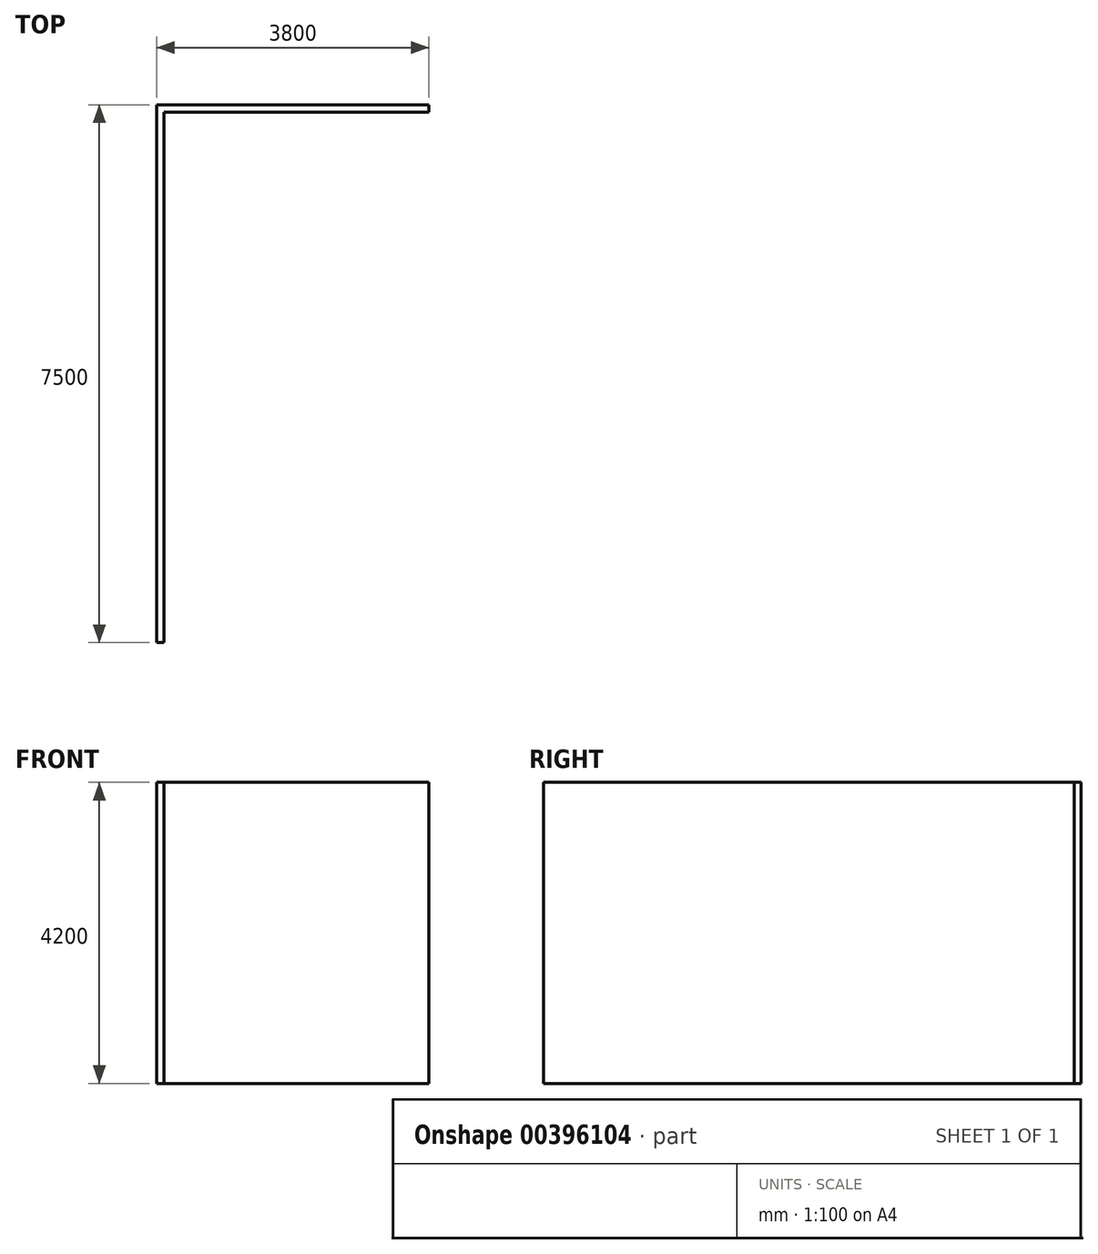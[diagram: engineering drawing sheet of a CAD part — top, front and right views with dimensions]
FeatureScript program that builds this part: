
annotation { "Feature Type Name" : "Feature", "Feature Type Description" : "" }
export const myFeature = defineFeature(function(context is Context, id is Id, definition is map)
    precondition{}
    {
        {
            var Q0;
            Q0=qCreatedBy(makeId("Top.planeOp"),FACE);
            var sketch = newSketch(context, id + "F0", { "sketchPlane" : qUnion([Q0])});
            skLineSegment(sketch, "E0", {"start": v(0, 0) * mm, "end": v(0, 7500) * mm});
            skLineSegment(sketch, "E1", {"start": v(0, 7500) * mm, "end": v(3800, 7500) * mm});
            skLineSegment(sketch, "E2", {"start": v(3800, 7500) * mm, "end": v(3800, 7400) * mm});
            skLineSegment(sketch, "E3", {"start": v(3800, 7400) * mm, "end": v(100, 7400) * mm});
            skLineSegment(sketch, "E4", {"start": v(100, 7400) * mm, "end": v(100, 0) * mm});
            skLineSegment(sketch, "E5", {"start": v(100, 0) * mm, "end": v(0, 0) * mm});
            skSolve(sketch);
        }
        {
            var Q0;
            Q0=makeQuery(id+"F0.imprint","IMPRINT",FACE,{"disambiguationData":[TD([[makeQuery(id+"F0.imprint","IMPRINT",EDGE,{"derivedFrom":sQuery(id+"F0.wireOp",EDGE,"E0")}),-1.0]])]});
            extrude(context, id + "F1", {"entities" : qUnion([Q0]), "depth" : 4200 * mm});
        }
    });
